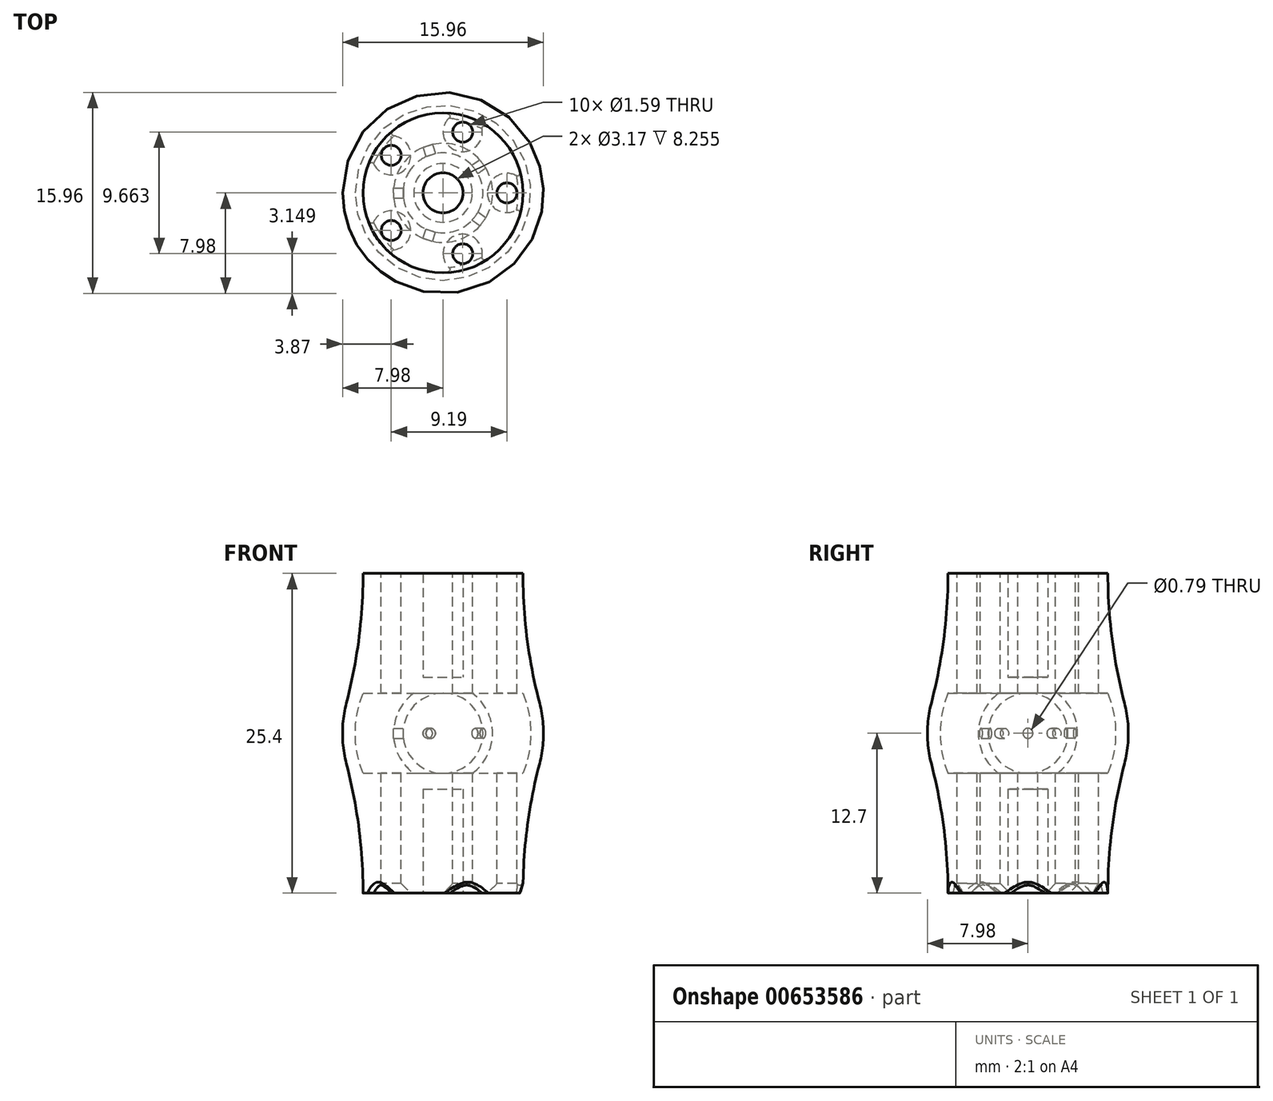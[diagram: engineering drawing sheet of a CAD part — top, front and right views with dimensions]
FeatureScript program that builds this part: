
annotation { "Feature Type Name" : "Feature", "Feature Type Description" : "" }
export const myFeature = defineFeature(function(context is Context, id is Id, definition is map)
    precondition{}
    {
        {
            var Q0;
            Q0=qCreatedBy(makeId("Front.planeOp"),FACE);
            var sketch = newSketch(context, id + "F0", { "sketchPlane" : qUnion([Q0])});
            skLineSegment(sketch, "E0", {"start": v(0, -51.33) * mm, "end": v(0, 86.3) * mm, "construction": true});
            skLineSegment(sketch, "E1", {"start": v(0, 8.26) * mm, "end": v(1.59, 8.26) * mm});
            skLineSegment(sketch, "E2", {"start": v(1.59, 8.25) * mm, "end": v(1.59, 0) * mm});
            skLineSegment(sketch, "E3", {"start": v(1.59, 0) * mm, "end": v(6.35, 0) * mm});
            skLineSegment(sketch, "E4", {"start": v(6.35, 0) * mm, "end": v(6.35, 7.37) * mm, "construction": true});
            skLineSegment(sketch, "E5", {"start": v(6.35, 18.03) * mm, "end": v(6.35, 25.4) * mm, "construction": true});
            skLineSegment(sketch, "E6", {"start": v(6.35, 25.4) * mm, "end": v(1.59, 25.4) * mm});
            skLineSegment(sketch, "E7", {"start": v(1.59, 25.4) * mm, "end": v(1.59, 17.14) * mm});
            skLineSegment(sketch, "E8", {"start": v(1.59, 17.14) * mm, "end": v(0, 17.14) * mm});
            skLineSegment(sketch, "E9", {"start": v(0, 17.15) * mm, "end": v(0, 15.88) * mm});
            skLineSegment(sketch, "E10", {"start": v(0, 15.88) * mm, "end": v(6.35, 15.88) * mm});
            skLineSegment(sketch, "E11", {"start": v(6.35, 9.53) * mm, "end": v(0, 9.53) * mm});
            skLineSegment(sketch, "E12", {"start": v(0, 9.53) * mm, "end": v(0, 8.26) * mm});
            skArc(sketch, "E13", {"start": v(7.67, 10.3) * mm, "mid": v(7.98, 12.7) * mm, "end": v(7.67, 15.1) * mm});
            skArc(sketch, "E14", {"start": v(6.35, 9.53) * mm, "mid": v(6.96, 12.7) * mm, "end": v(6.35, 15.88) * mm});
            skArc(sketch, "E15", {"start": v(6.35, 25.4) * mm, "mid": v(6.68, 20.21) * mm, "end": v(7.67, 15.1) * mm});
            skArc(sketch, "E16", {"start": v(7.67, 10.3) * mm, "mid": v(6.68, 5.19) * mm, "end": v(6.35, 0) * mm});
            skArc(sketch, "E17", {"start": v(0, 9.53) * mm, "mid": v(3.18, 12.7) * mm, "end": v(0, 15.88) * mm});
            skArc(sketch, "E18", {"start": v(2.33, 9.53) * mm, "mid": v(3.94, 12.7) * mm, "end": v(2.33, 15.88) * mm});
            skSolve(sketch);
        }
        {
            var Q0;
            Q0=makeQuery(id+"F0.imprint","IMPRINT",FACE,{"disambiguationData":[TD([[makeQuery(id+"F0.imprint","IMPRINT",EDGE,{"derivedFrom":sQuery(id+"F0.wireOp",EDGE,"E1")}),1.0]])]});
            var Q1;
            {var subQ0=sQuery(id+"F0.wireOp",EDGE,"E17");Q1=makeQuery(id+"F0.imprint","IMPRINT",FACE,{"disambiguationData":[TD([[makeQuery(id+"F0.imprint","IMPRINT",EDGE,{"derivedFrom":subQ0}),-1.0]])]});}
            var Q2;
            Q2=sQuery(id+"F0.wireOp",EDGE,"E0");
            revolve(context, id + "F1", {"entities" : qUnion([Q0, Q1]), "axis" : qUnion([Q2]), "revolveType" : RevolveType.FULL});
        }
        {
            var Q0;
            Q0=makeQuery(id+"F1.opRevolve","SWEPT_FACE",FACE,{"disambiguationData":[OSD([sQuery(id+"F0.wireOp",EDGE,"E6")])]});
            var sketch = newSketch(context, id + "F2", { "sketchPlane" : qUnion([Q0])});
            skCircle(sketch, "E19", {"center": v(5.08, 0) * mm, "radius": 0.8 * mm});
            skCircle(sketch, "E20", {"center": v(0, 0) * mm, "radius": 5.08 * mm, "construction": true});
            skCircle(sketch, "E21.1.0", {"center": v(1.57, 4.83) * mm, "radius": 0.8 * mm});
            skCircle(sketch, "E21.2.0", {"center": v(-4.1, 2.99) * mm, "radius": 0.8 * mm});
            skCircle(sketch, "E22.1.3.0", {"center": v(-4.1, -2.99) * mm, "radius": 0.8 * mm});
            skCircle(sketch, "E22.1.4.0", {"center": v(1.57, -4.83) * mm, "radius": 0.8 * mm});
            skSolve(sketch);
        }
        {
            var Q0;
            Q0=makeQuery(id+"F2.imprint","IMPRINT",FACE,{"disambiguationData":[TD([[makeQuery(id+"F2.imprint","IMPRINT",EDGE,{"derivedFrom":sQuery(id+"F2.wireOp",EDGE,"E19")}),1.0]])]});
            var Q1;
            Q1=makeQuery(id+"F2.imprint","IMPRINT",FACE,{"disambiguationData":[TD([[makeQuery(id+"F2.imprint","IMPRINT",EDGE,{"derivedFrom":sQuery(id+"F2.wireOp",EDGE,"E21.1.0")}),1.0]])]});
            var Q2;
            Q2=makeQuery(id+"F2.imprint","IMPRINT",FACE,{"disambiguationData":[TD([[makeQuery(id+"F2.imprint","IMPRINT",EDGE,{"derivedFrom":sQuery(id+"F2.wireOp",EDGE,"E22.1.3.0")}),1.0]])]});
            var Q3;
            Q3=makeQuery(id+"F2.imprint","IMPRINT",FACE,{"disambiguationData":[TD([[makeQuery(id+"F2.imprint","IMPRINT",EDGE,{"derivedFrom":sQuery(id+"F2.wireOp",EDGE,"E22.1.4.0")}),1.0]])]});
            var Q4;
            Q4=makeQuery(id+"F2.imprint","IMPRINT",FACE,{"disambiguationData":[TD([[makeQuery(id+"F2.imprint","IMPRINT",EDGE,{"derivedFrom":sQuery(id+"F2.wireOp",EDGE,"E21.2.0")}),1.0]])]});
            extrude(context, id + "F3", {"entities" : qUnion([Q0, Q1, Q2, Q3, Q4]), "operationType" : NewBodyOperationType.REMOVE, "endBound" : BoundingType.THROUGH_ALL, "oppositeDirection" : true, "depth" : 25.4 * mm, "offsetDistance" : 25.4 * mm});
        }
        {
            var Q0;
            Q0=qCreatedBy(makeId("Right.planeOp"),FACE);
            var sketch = newSketch(context, id + "F4", { "sketchPlane" : qUnion([Q0])});
            skCircle(sketch, "E23", {"center": v(0, 12.7) * mm, "radius": 0.4 * mm});
            skSolve(sketch);
        }
        {
            var Q0;
            Q0 = qSketchRegion(id + "F4", true);
            extrude(context, id + "F5", {"entities" : qUnion([Q0]), "oppositeDirection" : true, "depth" : 5.08 * mm, "offsetDistance" : 25.4 * mm});
        }
        {
            var Q0;
            Q0=makeQuery(id+"F5.opExtrude","SWEPT_BODY",BODY,{"disambiguationData":[OSD([sQuery(id+"F4.wireOp",EDGE,"E23")])]});
            var Q1;
            Q1=makeQuery(id+"F1.opRevolve","SWEPT_EDGE",EDGE,{"disambiguationData":[OSD([sQuery(id+"F0.wireOp",EDGE,"E6"),sQuery(id+"F0.wireOp",EDGE,"E7")])]});
            circularPattern(context, id + "F6", {"operationType" : NewBodyOperationType.REMOVE, "entities" : qUnion([Q0]), "axis" : qUnion([Q1]), "angle" : 360 * degree, "instanceCount" : 5, "equalSpace" : true});
        }
        {
            var Q0;
            Q0=makeQuery(id+"F3.boolean.opBoolean","COPY",EDGE,{"derivedFrom":makeQuery(id+"F3.opExtrude","CAP_EDGE",EDGE,{"disambiguationData":[OSD([sQuery(id+"F2.wireOp",EDGE,"E21.2.0")])],"isStart":true})});
            var Q1;
            Q1=makeQuery(id+"F3.boolean.opBoolean","COPY",EDGE,{"derivedFrom":makeQuery(id+"F3.opExtrude","CAP_EDGE",EDGE,{"disambiguationData":[OSD([sQuery(id+"F2.wireOp",EDGE,"E22.1.3.0")])],"isStart":true})});
            var Q2;
            Q2=makeQuery(id+"F3.boolean.opBoolean","COPY",EDGE,{"derivedFrom":makeQuery(id+"F3.opExtrude","CAP_EDGE",EDGE,{"disambiguationData":[OSD([sQuery(id+"F2.wireOp",EDGE,"E22.1.4.0")])],"isStart":true})});
            var Q3;
            Q3=makeQuery(id+"F3.boolean.opBoolean","COPY",EDGE,{"derivedFrom":makeQuery(id+"F3.opExtrude","CAP_EDGE",EDGE,{"disambiguationData":[OSD([sQuery(id+"F2.wireOp",EDGE,"E19")])],"isStart":true})});
            var Q4;
            Q4=makeQuery(id+"F3.boolean.opBoolean","COPY",EDGE,{"derivedFrom":makeQuery(id+"F3.opExtrude","CAP_EDGE",EDGE,{"disambiguationData":[OSD([sQuery(id+"F2.wireOp",EDGE,"E21.1.0")])],"isStart":true})});
            var Q5;
            Q5=makeQuery(id+"F3.boolean.opBoolean","INTERSECT",EDGE,{"derivedFrom":[makeQuery(id+"F1.opRevolve","SWEPT_FACE",FACE,{"disambiguationData":[OSD([sQuery(id+"F0.wireOp",EDGE,"E3")])]}),makeQuery(id+"F3.opExtrude","SWEPT_FACE",FACE,{"disambiguationData":[OSD([sQuery(id+"F2.wireOp",EDGE,"E22.1.4.0")])]})]});
            var Q6;
            Q6=makeQuery(id+"F3.boolean.opBoolean","INTERSECT",EDGE,{"derivedFrom":[makeQuery(id+"F1.opRevolve","SWEPT_FACE",FACE,{"disambiguationData":[OSD([sQuery(id+"F0.wireOp",EDGE,"E3")])]}),makeQuery(id+"F3.opExtrude","SWEPT_FACE",FACE,{"disambiguationData":[OSD([sQuery(id+"F2.wireOp",EDGE,"E22.1.3.0")])]})]});
            var Q7;
            Q7=makeQuery(id+"F3.boolean.opBoolean","INTERSECT",EDGE,{"derivedFrom":[makeQuery(id+"F1.opRevolve","SWEPT_FACE",FACE,{"disambiguationData":[OSD([sQuery(id+"F0.wireOp",EDGE,"E3")])]}),makeQuery(id+"F3.opExtrude","SWEPT_FACE",FACE,{"disambiguationData":[OSD([sQuery(id+"F2.wireOp",EDGE,"E19")])]})]});
            var Q8;
            Q8=makeQuery(id+"F3.boolean.opBoolean","INTERSECT",EDGE,{"derivedFrom":[makeQuery(id+"F1.opRevolve","SWEPT_FACE",FACE,{"disambiguationData":[OSD([sQuery(id+"F0.wireOp",EDGE,"E3")])]}),makeQuery(id+"F3.opExtrude","SWEPT_FACE",FACE,{"disambiguationData":[OSD([sQuery(id+"F2.wireOp",EDGE,"E21.1.0")])]})]});
            var Q9;
            Q9=makeQuery(id+"F3.boolean.opBoolean","INTERSECT",EDGE,{"derivedFrom":[makeQuery(id+"F1.opRevolve","SWEPT_FACE",FACE,{"disambiguationData":[OSD([sQuery(id+"F0.wireOp",EDGE,"E3")])]}),makeQuery(id+"F3.opExtrude","SWEPT_FACE",FACE,{"disambiguationData":[OSD([sQuery(id+"F2.wireOp",EDGE,"E21.2.0")])]})]});
            chamfer(context, id + "F7", {"entities" : qUnion([Q0, Q1, Q2, Q3, Q4, Q5, Q6, Q7, Q8, Q9]), "width" : 0.76 * mm, "tangentPropagation" : true});
        }
        {
            var Q0;
            Q0=makeQuery(id+"F1.opRevolve","SWEPT_FACE",FACE,{"disambiguationData":[OSD([sQuery(id+"F0.wireOp",EDGE,"E8")])]});
            var sketch = newSketch(context, id + "F8", { "sketchPlane" : qUnion([Q0])});
            skCircle(sketch, "E24", {"center": v(0, 0) * mm, "radius": 1.64 * mm});
            skSolve(sketch);
        }
        {
            var Q0;
            Q0=makeQuery(id+"F8.imprint","IMPRINT",FACE,{"disambiguationData":[TD([[makeQuery(id+"F8.imprint","IMPRINT",EDGE,{"derivedFrom":sQuery(id+"F8.wireOp",EDGE,"E24")}),1.0]])]});
            var Q1;
            Q1=makeQuery(id+"F8.imprint","IMPRINT",FACE,{"disambiguationData":[TD([[makeQuery(id+"F8.imprint","IMPRINT",EDGE,{"derivedFrom":makeQuery(id+"F1.opRevolve","SWEPT_EDGE",EDGE,{"disambiguationData":[OSD([sQuery(id+"F0.wireOp",EDGE,"E7"),sQuery(id+"F0.wireOp",EDGE,"E8")])]})}),-1.0]])]});
            extrude(context, id + "F9", {"entities" : qUnion([Q0, Q1]), "depth" : 19.05 * mm, "offsetDistance" : 25.4 * mm});
        }
        {
            var Q0;
            Q0=makeQuery(id+"F7.opChamfer","BLEND_EDGE",EDGE,{"blendedFrom":[makeQuery(id+"F3.boolean.opBoolean","COPY",EDGE,{"derivedFrom":makeQuery(id+"F3.opExtrude","CAP_EDGE",EDGE,{"disambiguationData":[OSD([sQuery(id+"F2.wireOp",EDGE,"E19")])],"isStart":true})}),makeQuery(id+"F1.opRevolve","SWEPT_FACE",FACE,{"disambiguationData":[OSD([sQuery(id+"F0.wireOp",EDGE,"E15")])]})],"blendedInto":[makeQuery(id+"F1.opRevolve","SWEPT_FACE",FACE,{"disambiguationData":[OSD([sQuery(id+"F0.wireOp",EDGE,"E15")])]})]});
            var Q1;
            Q1=makeQuery(id+"F7.opChamfer","BLEND_EDGE",EDGE,{"blendedFrom":[makeQuery(id+"F3.boolean.opBoolean","COPY",EDGE,{"derivedFrom":makeQuery(id+"F3.opExtrude","CAP_EDGE",EDGE,{"disambiguationData":[OSD([sQuery(id+"F2.wireOp",EDGE,"E21.1.0")])],"isStart":true})}),makeQuery(id+"F1.opRevolve","SWEPT_FACE",FACE,{"disambiguationData":[OSD([sQuery(id+"F0.wireOp",EDGE,"E15")])]})],"blendedInto":[makeQuery(id+"F1.opRevolve","SWEPT_FACE",FACE,{"disambiguationData":[OSD([sQuery(id+"F0.wireOp",EDGE,"E15")])]})]});
            var Q2;
            Q2=makeQuery(id+"F7.opChamfer","BLEND_EDGE",EDGE,{"blendedFrom":[makeQuery(id+"F3.boolean.opBoolean","COPY",EDGE,{"derivedFrom":makeQuery(id+"F3.opExtrude","CAP_EDGE",EDGE,{"disambiguationData":[OSD([sQuery(id+"F2.wireOp",EDGE,"E22.1.4.0")])],"isStart":true})}),makeQuery(id+"F1.opRevolve","SWEPT_FACE",FACE,{"disambiguationData":[OSD([sQuery(id+"F0.wireOp",EDGE,"E15")])]})],"blendedInto":[makeQuery(id+"F1.opRevolve","SWEPT_FACE",FACE,{"disambiguationData":[OSD([sQuery(id+"F0.wireOp",EDGE,"E15")])]})]});
            var Q3;
            Q3=makeQuery(id+"F7.opChamfer","BLEND_EDGE",EDGE,{"blendedFrom":[makeQuery(id+"F3.boolean.opBoolean","COPY",EDGE,{"derivedFrom":makeQuery(id+"F3.opExtrude","CAP_EDGE",EDGE,{"disambiguationData":[OSD([sQuery(id+"F2.wireOp",EDGE,"E21.2.0")])],"isStart":true})}),makeQuery(id+"F1.opRevolve","SWEPT_FACE",FACE,{"disambiguationData":[OSD([sQuery(id+"F0.wireOp",EDGE,"E15")])]})],"blendedInto":[makeQuery(id+"F1.opRevolve","SWEPT_FACE",FACE,{"disambiguationData":[OSD([sQuery(id+"F0.wireOp",EDGE,"E15")])]})]});
            var Q4;
            Q4=makeQuery(id+"F7.opChamfer","BLEND_EDGE",EDGE,{"blendedFrom":[makeQuery(id+"F3.boolean.opBoolean","COPY",EDGE,{"derivedFrom":makeQuery(id+"F3.opExtrude","CAP_EDGE",EDGE,{"disambiguationData":[OSD([sQuery(id+"F2.wireOp",EDGE,"E22.1.3.0")])],"isStart":true})}),makeQuery(id+"F1.opRevolve","SWEPT_FACE",FACE,{"disambiguationData":[OSD([sQuery(id+"F0.wireOp",EDGE,"E15")])]})],"blendedInto":[makeQuery(id+"F1.opRevolve","SWEPT_FACE",FACE,{"disambiguationData":[OSD([sQuery(id+"F0.wireOp",EDGE,"E15")])]})]});
            var Q5;
            Q5=makeQuery(id+"F7.opChamfer","BLEND_EDGE",EDGE,{"blendedFrom":[makeQuery(id+"F3.boolean.opBoolean","INTERSECT",EDGE,{"derivedFrom":[makeQuery(id+"F1.opRevolve","SWEPT_FACE",FACE,{"disambiguationData":[OSD([sQuery(id+"F0.wireOp",EDGE,"E3")])]}),makeQuery(id+"F3.opExtrude","SWEPT_FACE",FACE,{"disambiguationData":[OSD([sQuery(id+"F2.wireOp",EDGE,"E22.1.3.0")])]})]}),makeQuery(id+"F1.opRevolve","SWEPT_FACE",FACE,{"disambiguationData":[OSD([sQuery(id+"F0.wireOp",EDGE,"E16")])]})],"blendedInto":[makeQuery(id+"F1.opRevolve","SWEPT_FACE",FACE,{"disambiguationData":[OSD([sQuery(id+"F0.wireOp",EDGE,"E16")])]})]});
            var Q6;
            Q6=makeQuery(id+"F7.opChamfer","BLEND_EDGE",EDGE,{"blendedFrom":[makeQuery(id+"F3.boolean.opBoolean","INTERSECT",EDGE,{"derivedFrom":[makeQuery(id+"F1.opRevolve","SWEPT_FACE",FACE,{"disambiguationData":[OSD([sQuery(id+"F0.wireOp",EDGE,"E3")])]}),makeQuery(id+"F3.opExtrude","SWEPT_FACE",FACE,{"disambiguationData":[OSD([sQuery(id+"F2.wireOp",EDGE,"E21.2.0")])]})]}),makeQuery(id+"F1.opRevolve","SWEPT_FACE",FACE,{"disambiguationData":[OSD([sQuery(id+"F0.wireOp",EDGE,"E16")])]})],"blendedInto":[makeQuery(id+"F1.opRevolve","SWEPT_FACE",FACE,{"disambiguationData":[OSD([sQuery(id+"F0.wireOp",EDGE,"E16")])]})]});
            var Q7;
            Q7=makeQuery(id+"F7.opChamfer","BLEND_EDGE",EDGE,{"blendedFrom":[makeQuery(id+"F3.boolean.opBoolean","INTERSECT",EDGE,{"derivedFrom":[makeQuery(id+"F1.opRevolve","SWEPT_FACE",FACE,{"disambiguationData":[OSD([sQuery(id+"F0.wireOp",EDGE,"E3")])]}),makeQuery(id+"F3.opExtrude","SWEPT_FACE",FACE,{"disambiguationData":[OSD([sQuery(id+"F2.wireOp",EDGE,"E21.1.0")])]})]}),makeQuery(id+"F1.opRevolve","SWEPT_FACE",FACE,{"disambiguationData":[OSD([sQuery(id+"F0.wireOp",EDGE,"E16")])]})],"blendedInto":[makeQuery(id+"F1.opRevolve","SWEPT_FACE",FACE,{"disambiguationData":[OSD([sQuery(id+"F0.wireOp",EDGE,"E16")])]})]});
            var Q8;
            Q8=makeQuery(id+"F7.opChamfer","BLEND_EDGE",EDGE,{"blendedFrom":[makeQuery(id+"F3.boolean.opBoolean","INTERSECT",EDGE,{"derivedFrom":[makeQuery(id+"F1.opRevolve","SWEPT_FACE",FACE,{"disambiguationData":[OSD([sQuery(id+"F0.wireOp",EDGE,"E3")])]}),makeQuery(id+"F3.opExtrude","SWEPT_FACE",FACE,{"disambiguationData":[OSD([sQuery(id+"F2.wireOp",EDGE,"E22.1.4.0")])]})]}),makeQuery(id+"F1.opRevolve","SWEPT_FACE",FACE,{"disambiguationData":[OSD([sQuery(id+"F0.wireOp",EDGE,"E16")])]})],"blendedInto":[makeQuery(id+"F1.opRevolve","SWEPT_FACE",FACE,{"disambiguationData":[OSD([sQuery(id+"F0.wireOp",EDGE,"E16")])]})]});
            var Q9;
            Q9=makeQuery(id+"F7.opChamfer","BLEND_EDGE",EDGE,{"blendedFrom":[makeQuery(id+"F3.boolean.opBoolean","INTERSECT",EDGE,{"derivedFrom":[makeQuery(id+"F1.opRevolve","SWEPT_FACE",FACE,{"disambiguationData":[OSD([sQuery(id+"F0.wireOp",EDGE,"E3")])]}),makeQuery(id+"F3.opExtrude","SWEPT_FACE",FACE,{"disambiguationData":[OSD([sQuery(id+"F2.wireOp",EDGE,"E19")])]})]}),makeQuery(id+"F1.opRevolve","SWEPT_FACE",FACE,{"disambiguationData":[OSD([sQuery(id+"F0.wireOp",EDGE,"E16")])]})],"blendedInto":[makeQuery(id+"F1.opRevolve","SWEPT_FACE",FACE,{"disambiguationData":[OSD([sQuery(id+"F0.wireOp",EDGE,"E16")])]})]});
            fillet(context, id + "F10", {"entities" : qUnion([Q0, Q1, Q2, Q3, Q4, Q5, Q6, Q7, Q8, Q9]), "radius" : 0.25 * mm, "tangentPropagation" : true, "allowEdgeOverflow" : false});
        }
        {
            var Q0;
            Q0=makeQuery(id+"F9.opExtrude","CAP_EDGE",EDGE,{"disambiguationData":[OSD([sQuery(id+"F8.wireOp",EDGE,"E24")])],"isStart":false});
            chamfer(context, id + "F11", {"entities" : qUnion([Q0]), "width" : 0.76 * mm, "tangentPropagation" : true});
        }
        {
            var Q0;
            Q0=makeQuery(id+"F1.opRevolve","SWEPT_FACE",FACE,{"disambiguationData":[OSD([sQuery(id+"F0.wireOp",EDGE,"E6")])]});
            var Q1;
            Q1=makeQuery(id+"F1.opRevolve","SWEPT_FACE",FACE,{"disambiguationData":[OSD([sQuery(id+"F0.wireOp",EDGE,"E3")])]});
            cPlane(context, id + "F12", {"entities" : qUnion([Q0, Q1]), "cplaneType" : CPlaneType.MID_PLANE, "offset" : 25.4 * mm, "width" : 152.4 * mm, "height" : 152.4 * mm});
        }
        {
            var Q0;
            Q0=makeQuery(id+"F9.opExtrude","SWEPT_BODY",BODY,{"disambiguationData":[OSD([sQuery(id+"F8.wireOp",EDGE,"E24")])]});
            var Q1;
            Q1=qCreatedBy(id+"F12.planeOp",FACE);
            mirror(context, id + "F13", {"entities" : qUnion([Q0]), "mirrorPlane" : qUnion([Q1])});
        }
        {
            var Q0;
            Q0=makeQuery(id+"F9.opExtrude","SWEPT_BODY",BODY,{"disambiguationData":[OSD([sQuery(id+"F8.wireOp",EDGE,"E24")])]});
            var Q1;
            Q1=makeQuery(id+"F13.opPattern","COPY",BODY,{"derivedFrom":makeQuery(id+"F9.opExtrude","SWEPT_BODY",BODY,{"disambiguationData":[OSD([sQuery(id+"F8.wireOp",EDGE,"E24")])]}),"instanceName":"1"});
            deleteBodies(context, id + "F14", {"entities" : qUnion([Q0, Q1])});
        }
    });
